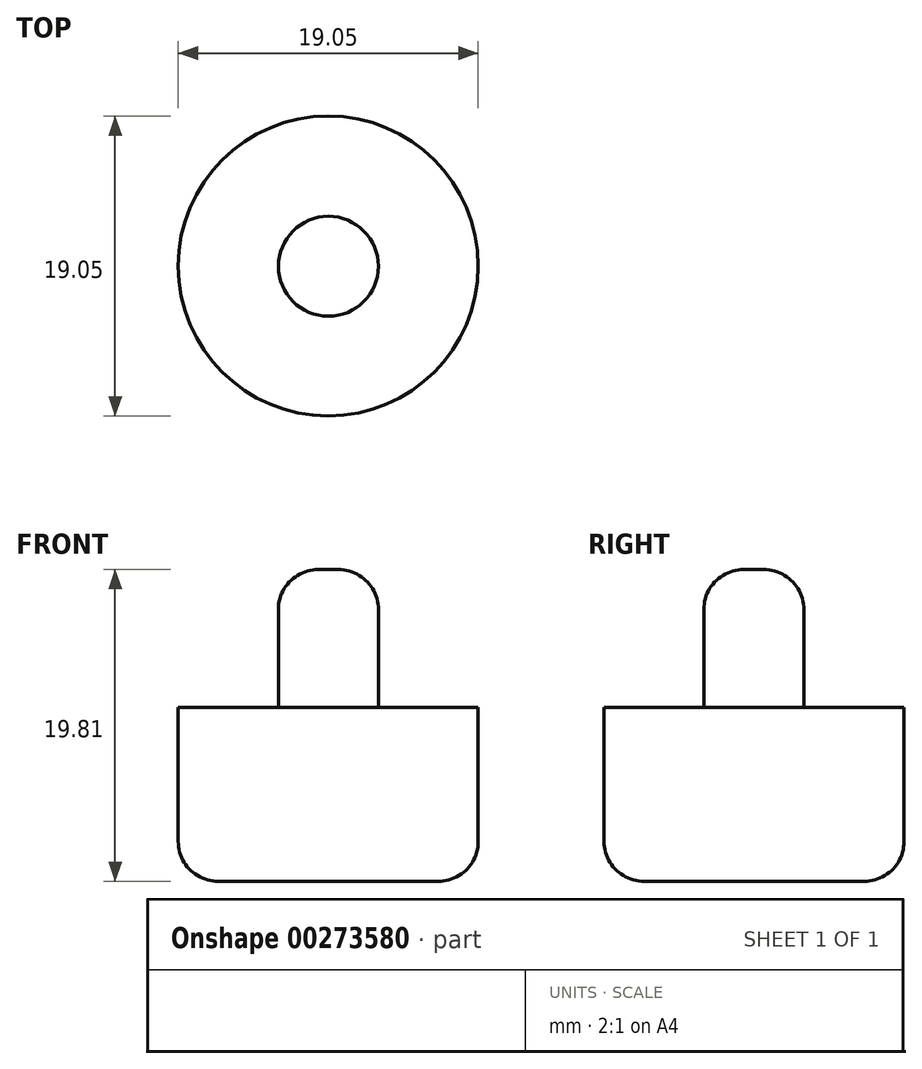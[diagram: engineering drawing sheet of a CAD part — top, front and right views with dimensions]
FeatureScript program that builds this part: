
annotation { "Feature Type Name" : "Feature", "Feature Type Description" : "" }
export const myFeature = defineFeature(function(context is Context, id is Id, definition is map)
    precondition{}
    {
        {
            var Q0;
            Q0=qCreatedBy(makeId("Top.planeOp"),FACE);
            var sketch = newSketch(context, id + "F0", { "sketchPlane" : qUnion([Q0])});
            skPoint(sketch, "E0.middle", {"position": v(0, 0) * mm});
            skCircle(sketch, "E1", {"center": v(-0.01, 0.02) * mm, "radius": 9.53 * mm});
            skSolve(sketch);
        }
        {
            var Q0;
            Q0=makeQuery(id+"F0.imprint","IMPRINT",FACE,{"disambiguationData":[TD([[makeQuery(id+"F0.imprint","IMPRINT",EDGE,{"derivedFrom":sQuery(id+"F0.wireOp",EDGE,"E1")}),1.0]])]});
            extrude(context, id + "F1", {"entities" : qUnion([Q0]), "depth" : 11.05 * mm});
        }
        {
            var Q0;
            Q0=makeQuery(id+"F1.opExtrude","CAP_EDGE",EDGE,{"disambiguationData":[OSD([sQuery(id+"F0.wireOp",EDGE,"E1")])],"isStart":true});
            fillet(context, id + "F2", {"entities" : qUnion([Q0]), "radius" : 2.54 * mm, "tangentPropagation" : true, "allowEdgeOverflow" : false});
        }
        {
            var Q0;
            Q0=makeQuery(id+"F1.opExtrude","CAP_FACE",FACE,{"disambiguationData":[OSD([sQuery(id+"F0.wireOp",EDGE,"E1")])],"isStart":false});
            var sketch = newSketch(context, id + "F3", { "sketchPlane" : qUnion([Q0])});
            skCircle(sketch, "E2", {"center": v(0, 0) * mm, "radius": 3.18 * mm});
            skSolve(sketch);
        }
        {
            var Q0;
            Q0=makeQuery(id+"F3.imprint","IMPRINT",FACE,{"disambiguationData":[TD([[makeQuery(id+"F3.imprint","IMPRINT",EDGE,{"derivedFrom":sQuery(id+"F3.wireOp",EDGE,"E2")}),1.0]])]});
            extrude(context, id + "F4", {"entities" : qUnion([Q0]), "operationType" : NewBodyOperationType.ADD, "depth" : 8.76 * mm});
        }
        {
            var Q0;
            Q0=makeQuery(id+"F4.opExtrude","CAP_EDGE",EDGE,{"disambiguationData":[OSD([sQuery(id+"F3.wireOp",EDGE,"E2")])],"isStart":false});
            var Q1;
            Q1=makeQuery(id+"F4.opExtrude","CAP_EDGE",EDGE,{"disambiguationData":[OSD([sQuery(id+"F3.wireOp",EDGE,"gvNMtX0L-LxiN-Eyd3-YDyU-Ib7kp0yB203n")])],"isStart":false});
            fillet(context, id + "F5", {"entities" : qUnion([Q0, Q1]), "radius" : 2.54 * mm, "tangentPropagation" : true, "allowEdgeOverflow" : false});
        }
    });
